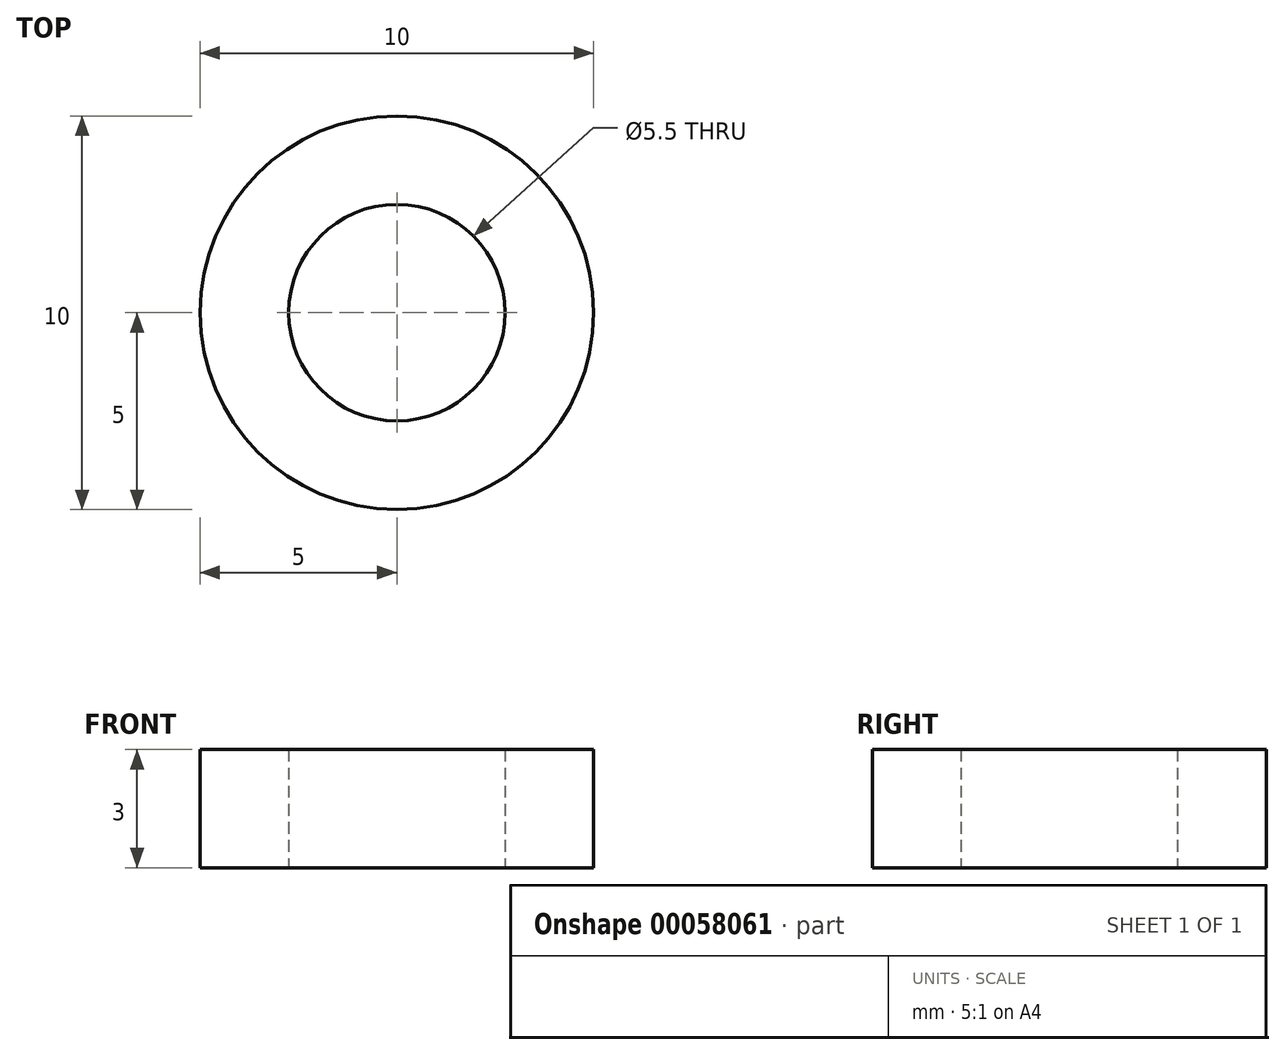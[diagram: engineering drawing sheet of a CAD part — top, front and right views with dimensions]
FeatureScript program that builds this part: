
annotation { "Feature Type Name" : "Feature", "Feature Type Description" : "" }
export const myFeature = defineFeature(function(context is Context, id is Id, definition is map)
    precondition{}
    {
        {
            var Q0;
            Q0=qCreatedBy(makeId("Top.planeOp"),FACE);
            var sketch = newSketch(context, id + "F0", { "sketchPlane" : qUnion([Q0])});
            skCircle(sketch, "E0", {"center": v(0, 0) * mm, "radius": 2.75 * mm});
            skCircle(sketch, "E1", {"center": v(0, 0) * mm, "radius": 5 * mm});
            skSolve(sketch);
        }
        {
            var Q0;
            Q0=makeQuery(id+"F0.imprint","IMPRINT",FACE,{"disambiguationData":[TD([[makeQuery(id+"F0.imprint","IMPRINT",EDGE,{"derivedFrom":sQuery(id+"F0.wireOp",EDGE,"E0")}),-1.0]])]});
            extrude(context, id + "F1", {"entities" : qUnion([Q0]), "depth" : 3 * mm});
        }
    });
